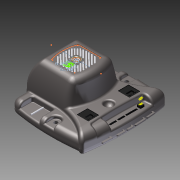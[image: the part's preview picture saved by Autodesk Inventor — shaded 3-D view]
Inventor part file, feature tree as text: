
AUTODESK INVENTOR PART (.ipt)
format: ipt  version: 2011 (Build 150239000, 239)  size: 3,075,072 bytes
history: native  units: mm
features: other x14, sketch x10, extrude x9, plane x5, mirror x3, imported_body x1
ambient origin geometry x8: Origin, YZ Plane, XZ Plane, XY Plane, X Axis, Y Axis, Z Axis, Center Point
bodies: Solid1 (feature_tree)
feature tree (42):
  imported_body  "Base1"
  sketch  "Sketch14"  dims[d87=2.286mm d88=4.572mm d89=4.572mm d90=3.81mm d91=0.0mm d92=-15.24mm d105=129.575698mm d160=0.254mm d162=1.27mm d169=0.635mm d182=1.27mm d183=0.0mm d187=6.35mm d188=0.0mm d191=6.35mm d192=6.35mm d193=6.35mm d214=7.9375mm d238=7.9375mm d239=7.9375mm d244=3.96875mm d245=1.133929mm]
  sketch  "Sketch1"  dims[d50=0.9144mm d57=1.467403mm]
  extrude  "Extrusion2"  Depth=1.467403mm
  plane  "Work Plane1"
  mirror  "Mirror1"
  extrude  "Extrusion3"  Depth=1.467403mm
  sketch  "Sketch2"  dims[d58=1.467403mm d59=1.467403mm]
  extrude  "Extrusion4"  Depth=1.467403mm
  extrude  "Extrusion6"  Depth=1.467403mm
  extrude  "Extrusion7"  TaperAngle=90.0deg  [1 undecoded]
  mirror  "Mirror2"
  extrude  "Extrusion8"  Depth=9.7282mm
  mirror  "Mirror3"
  sketch  "Sketch5"  dims[d62=1.467403mm d63=1.467403mm]
  other  "Work Axis1"
  extrude  "Extrusion9"  Depth=0.762mm
  plane  "Work Plane2"
  extrude  "Extrusion10"  Depth=0.254mm TaperAngle=0.0deg
  extrude  "Extrusion12"  Depth=1.27mm
  sketch  "Sketch12"  dims[d80=2.54mm d81=0.0mm d82=0.254mm d83=0.0mm]
  other  "Work Point1"
  other  "Work Point2"
  other  "Work Point3"
  other  "Work Point7"
  other  "Work Point8"
  other  "Work Point9"
  other  "Decal1"
  sketch  "Sketch4"  dims[d60=1.467403mm d61=1.467403mm]
  sketch  "Sketch6"  dims[d66=1.27mm d67=0.0mm d70=90.0deg]
  sketch  "Sketch7"  dims[d71=1.27mm d72=0.0mm d73=9.7282mm]
  other  "Image2"
  sketch  "Sketch11"  dims[d75=0.762mm d76=0.0mm d77=0.762mm]
  plane  "Work Plane3"
  other  "Work Axis2"
  plane  "Work Plane4"
  other  "Work Axis3"
  plane  "Work Plane5"
  other  "Work Axis4"
  sketch  "Sketch13"  dims[d84=1.016mm d85=0.0mm d86=1.27mm]
  other  "Image4"
  other  "Image5"
note: 1 required parameter value undecoded (feature->parameter linkage not recoverable at this tier; creation-order binding heuristic only, values carry confidence <= 0.55)
